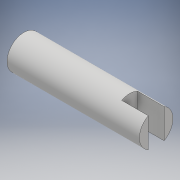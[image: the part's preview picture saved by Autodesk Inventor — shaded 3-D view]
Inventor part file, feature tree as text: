
AUTODESK INVENTOR PART (.ipt)
format: ipt  version: 2017 (Build 210142000, 142)  size: 100,864 bytes
history: native  units: mm
features: extrude x2, sketch x2
ambient origin geometry x8: Origin, YZ Plane, XZ Plane, XY Plane, X Axis, Y Axis, Z Axis, Center Point
bodies: Solid1 (feature_tree)
feature tree (4):
  extrude  "Extrusion1"  Depth=25.0mm TaperAngle=0.0deg
  extrude  "Extrusion2"  Depth=3.0mm
  sketch  "Sketch1"  dims[d0=6.35mm d1=25.0mm d2=0.0mm]
  sketch  "Sketch2"  dims[d3=10.0mm d4=3.0mm d5=5.0mm d6=0.0mm]
